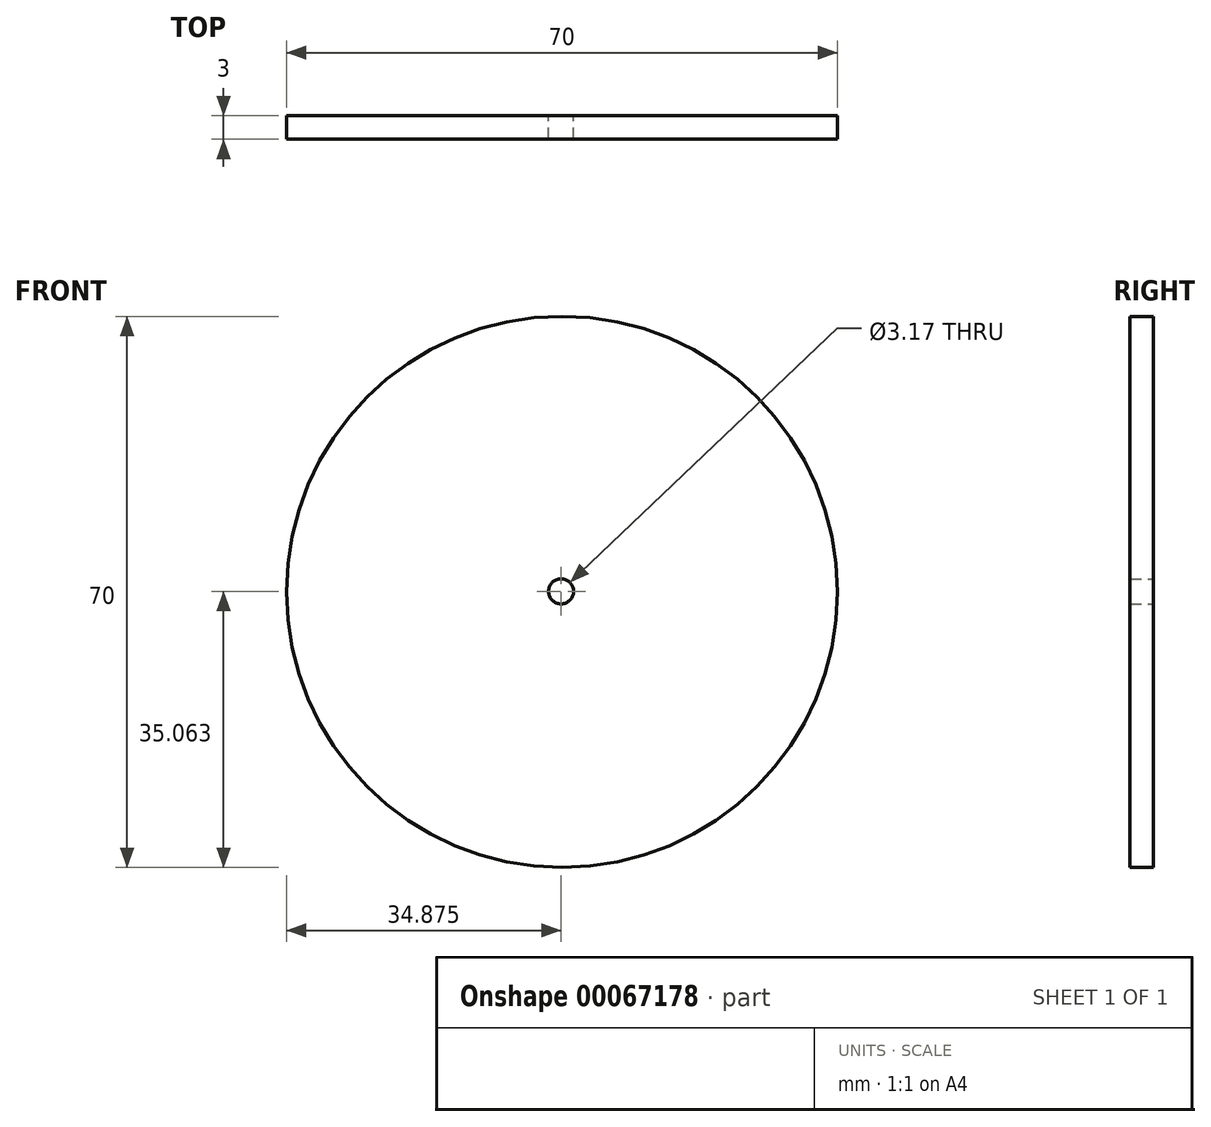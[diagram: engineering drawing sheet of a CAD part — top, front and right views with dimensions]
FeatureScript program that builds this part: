
annotation { "Feature Type Name" : "Feature", "Feature Type Description" : "" }
export const myFeature = defineFeature(function(context is Context, id is Id, definition is map)
    precondition{}
    {
        {
            var Q0;
            Q0=qCreatedBy(makeId("Front.planeOp"),FACE);
            var sketch = newSketch(context, id + "F0", { "sketchPlane" : qUnion([Q0])});
            skCircle(sketch, "E0", {"center": v(0, 0) * mm, "radius": 35 * mm});
            skCircle(sketch, "E1", {"center": v(-0.13, 0.06) * mm, "radius": 1.59 * mm});
            skSolve(sketch);
        }
        {
            var Q0;
            Q0=makeQuery(id+"F0.imprint","IMPRINT",FACE,{"disambiguationData":[TD([[makeQuery(id+"F0.imprint","IMPRINT",EDGE,{"derivedFrom":sQuery(id+"F0.wireOp",EDGE,"E0")}),1.0]])]});
            extrude(context, id + "F1", {"entities" : qUnion([Q0]), "depth" : 3 * mm});
        }
    });
